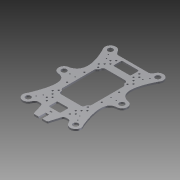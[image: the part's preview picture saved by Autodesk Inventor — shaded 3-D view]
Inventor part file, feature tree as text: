
AUTODESK INVENTOR PART (.ipt)
format: ipt  version: 2015 (Build 190159000, 159)  size: 535,552 bytes
history: native  units: mm
features: sketch x4, hole x3, extrude x2
ambient origin geometry x8: Origin, YZ Plane, XZ Plane, XY Plane, X Axis, Y Axis, Z Axis, Center Point
bodies: Solid1 (feature_tree)
feature tree (9):
  extrude  "Extrusion1"  Depth=3.0mm TaperAngle=0.0deg
  sketch  "Sketch2"  dims[d75=2.0mm d76=5.0mm d77=5.0mm d78=3.0mm d79=3.0mm d80=15.0mm d81=15.0mm d82=30.0mm d83=82.0mm d84=2.0mm d85=2.0mm d86=5.0mm d87=10.0mm d88=15.0mm d89=20.0mm d90=2.0mm d91=8.75mm d92=8.75mm d93=8.75mm d94=8.75mm d95=8.75mm d96=8.75mm d97=2.0mm d98=2.0mm d99=9.0mm d100=2.0mm d101=2.0mm d102=9.0mm d103=10.0mm d104=6.0mm d105=21.0mm d106=21.014083mm d107=21.014083mm d108=21.0mm d109=21.0mm d110=21.014083mm d111=21.0mm d112=21.014083mm d113=4.0mm d114=4.0mm d115=4.0mm d116=4.0mm d117=4.0mm d118=4.0mm d119=4.0mm d120=4.0mm d121=4.0mm d122=4.0mm d123=4.0mm d124=4.0mm d125=68.5mm d126=50.55mm d127=15.0mm d128=15.0mm d129=15.0mm d130=15.0mm d131=5.632993mm d132=10.75mm d133=10.0mm d134=10.0mm d135=4.7mm d136=5.0mm d137=5.0mm d138=5.0mm d139=10.8mm d140=10.0mm d141=4.7mm d142=5.0mm d143=5.0mm d144=10.0mm d145=5.0mm d146=5.0mm d147=5.682993mm d148=8.75mm d149=6.0mm d150=4.0mm d151=2.0mm d152=90.0deg d153=8.0mm d154=20.594885mm]
  hole  "Hole1"  [1 undecoded]
  hole  "Hole2"  [1 undecoded]
  hole  "Hole3"  [1 undecoded]
  extrude  "Extrusion2"  Depth=3.0mm
  sketch  "Sketch1"  dims[d0=2.0mm d1=5.0mm d2=5.0mm d5=15.0mm d6=15.0mm d7=30.0mm d8=82.0mm d9=2.0mm d10=2.0mm d12=10.0mm d13=15.0mm d14=20.0mm d15=2.0mm d29=6.0mm d38=4.0mm d39=4.0mm d40=4.0mm d42=4.0mm d44=4.0mm d45=4.0mm d46=4.0mm d47=4.0mm d48=4.0mm d49=4.0mm d73=3.0mm d74=0.0mm]
  sketch  "Sketch3"  dims[d155=2.0mm d156=5.0mm d157=5.0mm d158=3.0mm d159=3.0mm d160=15.0mm d161=15.0mm d162=30.0mm d163=82.0mm d164=2.0mm d165=2.0mm d166=5.0mm d167=10.0mm d168=15.0mm d169=20.0mm d170=2.0mm d171=8.75mm d172=8.75mm d173=8.75mm d174=8.75mm d175=8.75mm d176=8.75mm d177=2.0mm d178=2.0mm d179=9.0mm d180=2.0mm d181=2.0mm d182=9.0mm d183=10.0mm d184=6.0mm d185=21.0mm d186=21.014083mm d187=21.014083mm d188=21.0mm d189=21.0mm d190=21.014083mm d191=21.0mm d192=21.014083mm d193=4.0mm d194=4.0mm d195=4.0mm d196=4.0mm d197=4.0mm d198=4.0mm d199=4.0mm d200=4.0mm d201=4.0mm d202=4.0mm d203=4.0mm d204=4.0mm d205=68.5mm d206=50.55mm d207=15.0mm d208=15.0mm d209=15.0mm d210=15.0mm d211=5.632993mm d212=10.75mm d213=10.0mm d214=10.0mm d215=4.7mm d216=5.0mm d217=5.0mm d218=5.0mm d219=10.8mm d220=10.0mm d221=4.7mm d222=5.0mm d223=5.0mm d224=10.0mm d225=5.0mm d226=5.0mm d227=5.682993mm d228=3.0mm d229=6.0mm d230=4.0mm d231=2.0mm d232=90.0deg d233=8.0mm d234=20.594885mm]
  sketch  "Sketch4"  dims[d235=2.0mm d236=5.0mm d237=5.0mm d238=3.0mm d239=3.0mm d240=15.0mm d241=15.0mm d242=30.0mm d243=82.0mm d244=2.0mm d245=2.0mm d246=5.0mm d247=10.0mm d248=15.0mm d249=20.0mm d250=2.0mm d251=8.75mm d252=8.75mm d253=8.75mm d254=8.75mm d255=8.75mm d256=8.75mm d257=2.0mm d258=2.0mm d259=9.0mm d260=2.0mm d261=2.0mm d262=9.0mm d263=10.0mm d264=6.0mm d265=21.0mm d266=21.014083mm d267=21.014083mm d268=21.0mm d269=21.0mm d270=21.014083mm d271=21.0mm d272=21.014083mm d273=4.0mm d274=4.0mm d275=4.0mm d276=4.0mm d277=4.0mm d278=4.0mm d279=4.0mm d280=4.0mm d281=4.0mm d282=4.0mm d283=4.0mm d284=4.0mm d285=68.5mm d286=50.55mm d287=15.0mm d288=15.0mm d289=15.0mm d290=15.0mm d291=5.632993mm d292=10.75mm d293=10.0mm d294=10.0mm d295=4.7mm d296=5.0mm d297=5.0mm d298=5.0mm d299=10.8mm d300=10.0mm d301=4.7mm d302=5.0mm d303=5.0mm d304=10.0mm d305=5.0mm d306=5.0mm d307=5.682993mm d308=2.0mm d309=6.0mm d310=4.0mm d311=2.0mm d312=90.0deg d313=8.0mm d314=20.594885mm d324=3.0mm d325=0.0mm d326=50.55mm d327=68.5mm d328=50.55mm d329=68.5mm d330=50.55mm d331=68.5mm d332=3.0mm d333=5.0mm d334=5.0mm d335=3.0mm d336=12.0mm d337=5.0mm]
note: 3 required parameter values undecoded (feature->parameter linkage not recoverable at this tier; creation-order binding heuristic only, values carry confidence <= 0.55)
